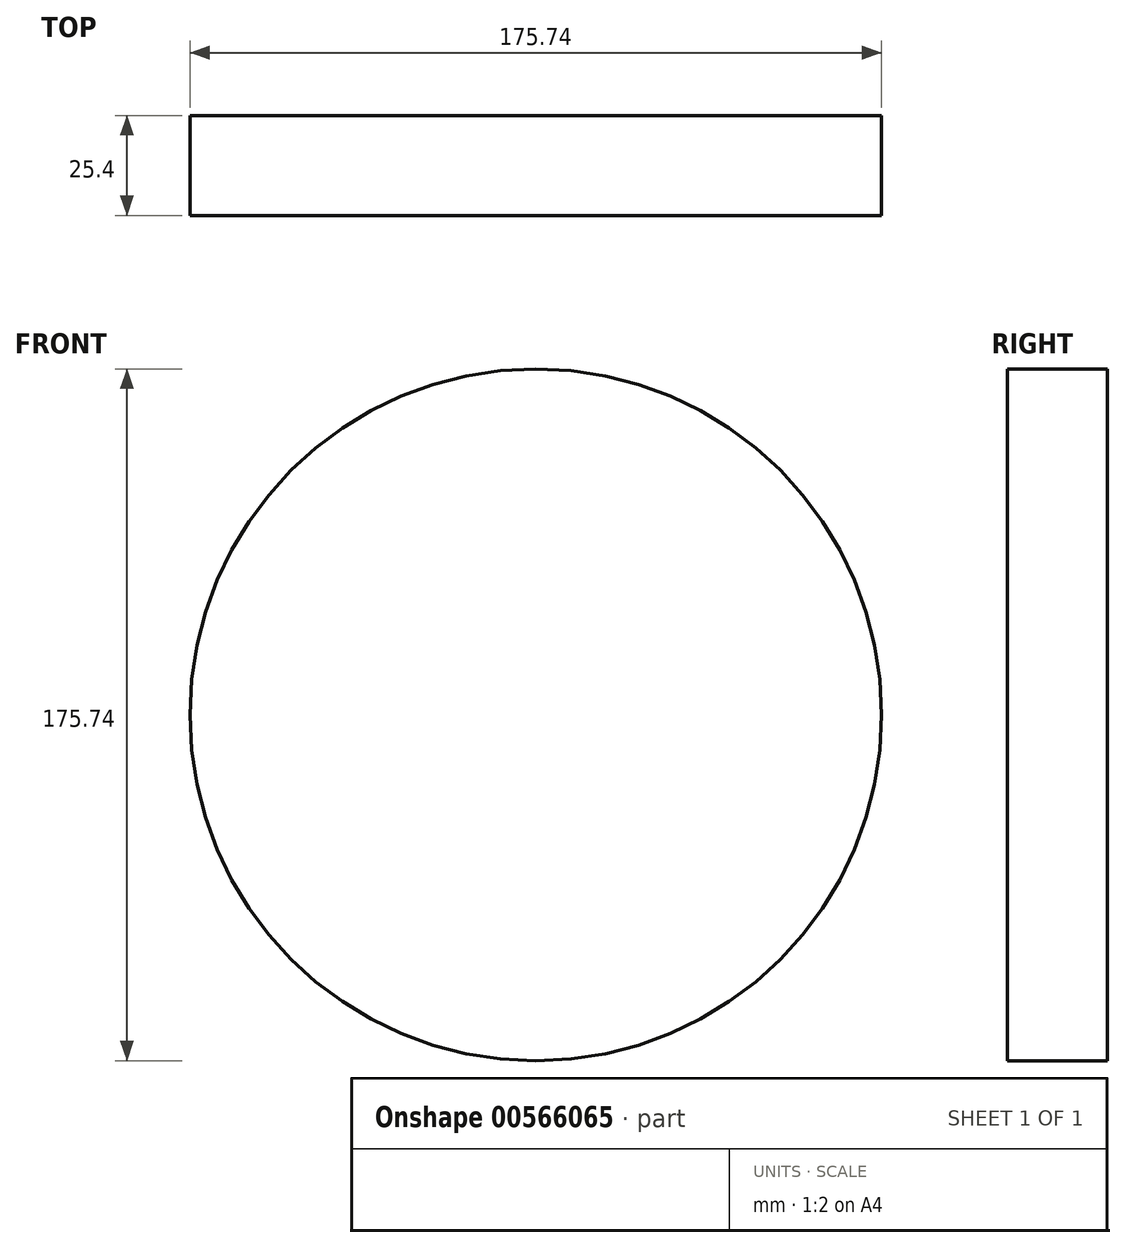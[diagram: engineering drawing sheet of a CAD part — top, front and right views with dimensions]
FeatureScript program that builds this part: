
annotation { "Feature Type Name" : "Feature", "Feature Type Description" : "" }
export const myFeature = defineFeature(function(context is Context, id is Id, definition is map)
    precondition{}
    {
        {
            var Q0;
            Q0=qCreatedBy(makeId("Front.planeOp"),FACE);
            var sketch = newSketch(context, id + "F0", { "sketchPlane" : qUnion([Q0])});
            skCircle(sketch, "E0", {"center": v(0, 0) * mm, "radius": 87.87 * mm});
            skSolve(sketch);
        }
        {
            var Q0;
            Q0=sQuery(id+"F0.wireOp",EDGE,"E0");
            extrude(context, id + "F1", {"bodyType" : ToolBodyType.SURFACE, "surfaceEntities" : qUnion([Q0]), "depth" : 25.4 * mm, "offsetDistance" : 25.4 * mm});
        }
    });
